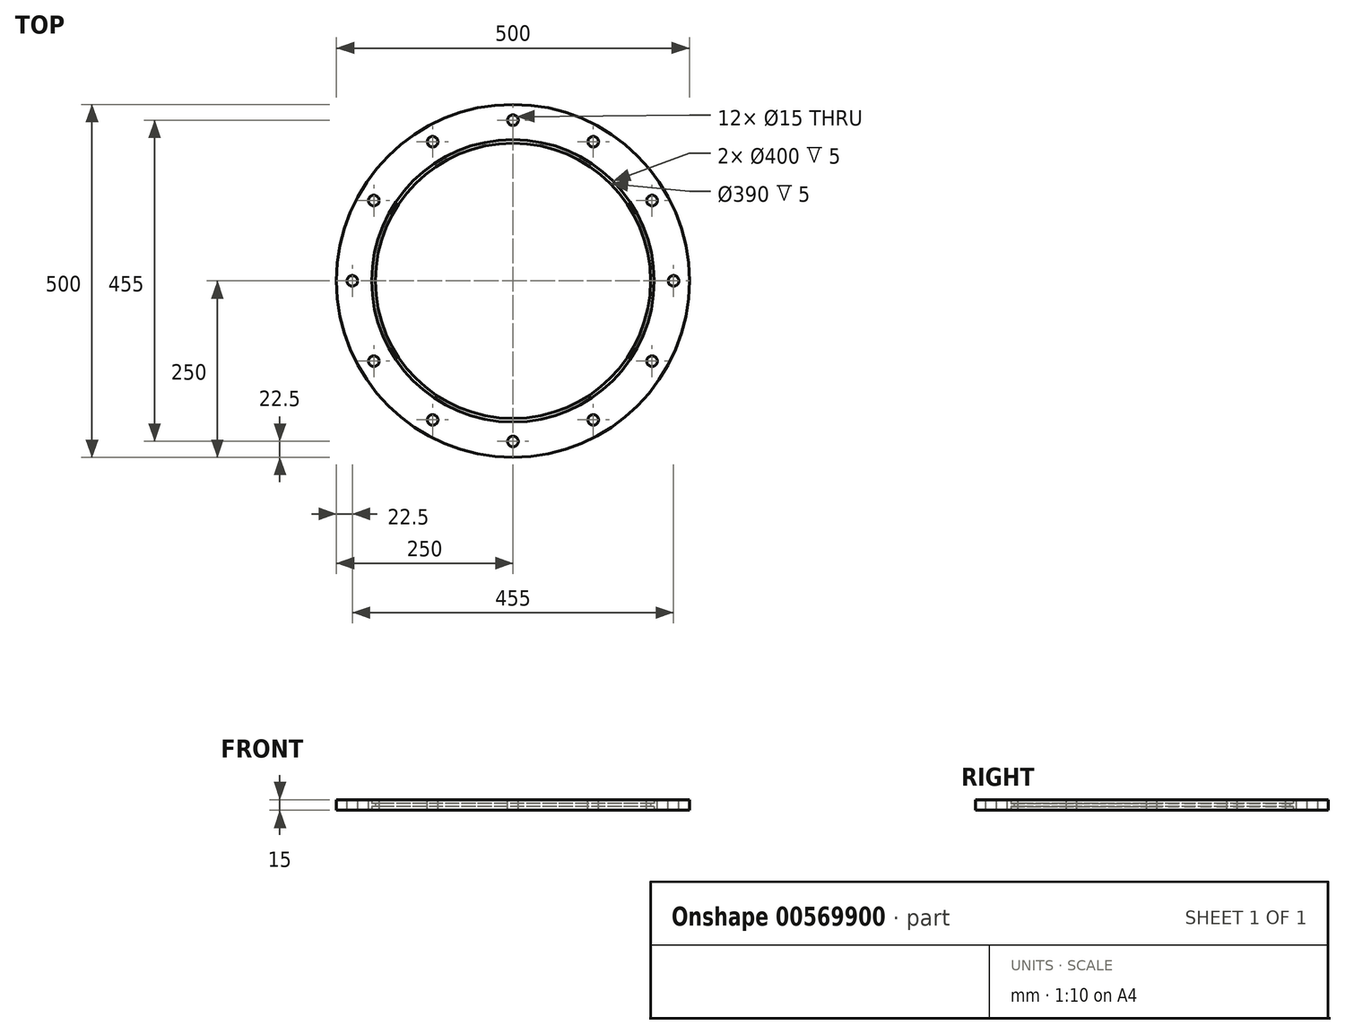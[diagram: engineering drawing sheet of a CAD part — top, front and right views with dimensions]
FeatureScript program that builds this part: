
annotation { "Feature Type Name" : "Feature", "Feature Type Description" : "" }
export const myFeature = defineFeature(function(context is Context, id is Id, definition is map)
    precondition{}
    {
        {
            var Q0;
            Q0=qCreatedBy(makeId("Top.planeOp"),FACE);
            var sketch = newSketch(context, id + "F0", { "sketchPlane" : qUnion([Q0])});
            skCircle(sketch, "E0", {"center": v(0, 0) * mm, "radius": 250 * mm});
            skCircle(sketch, "E1", {"center": v(0, 0) * mm, "radius": 200 * mm});
            skSolve(sketch);
        }
        {
            var Q0;
            Q0=qSketchRegion(id+"F0",true);
            extrude(context, id + "F1", {"entities" : qUnion([Q0]), "depth" : 15 * mm, "offsetDistance" : 25 * mm});
        }
        {
            var Q0;
            Q0=makeQuery(id+"F1.opExtrude","CAP_FACE",FACE,{"disambiguationData":[OSD([sQuery(id+"F0.wireOp",EDGE,"E0"),sQuery(id+"F0.wireOp",EDGE,"E1")])],"isStart":false});
            var sketch = newSketch(context, id + "F2", { "sketchPlane" : qUnion([Q0])});
            skCircle(sketch, "E2", {"center": v(227.5, 0) * mm, "radius": 7.5 * mm});
            skCircle(sketch, "E3.1.0", {"center": v(197.02, 113.75) * mm, "radius": 7.5 * mm});
            skCircle(sketch, "E3.2.0", {"center": v(113.75, 197.02) * mm, "radius": 7.5 * mm});
            skCircle(sketch, "E3.3.0", {"center": v(0, 227.5) * mm, "radius": 7.5 * mm});
            skCircle(sketch, "E3.4.0", {"center": v(-113.75, 197.02) * mm, "radius": 7.5 * mm});
            skCircle(sketch, "E3.5.0", {"center": v(-197.02, 113.75) * mm, "radius": 7.5 * mm});
            skCircle(sketch, "E3.6.0", {"center": v(-227.5, 0) * mm, "radius": 7.5 * mm});
            skCircle(sketch, "E3.7.0", {"center": v(-197.02, -113.75) * mm, "radius": 7.5 * mm});
            skCircle(sketch, "E3.8.0", {"center": v(-113.75, -197.02) * mm, "radius": 7.5 * mm});
            skCircle(sketch, "E3.9.0", {"center": v(0, -227.5) * mm, "radius": 7.5 * mm});
            skCircle(sketch, "E3.10.0", {"center": v(113.75, -197.02) * mm, "radius": 7.5 * mm});
            skCircle(sketch, "E3.11.0", {"center": v(197.02, -113.75) * mm, "radius": 7.5 * mm});
            skPoint(sketch, "E3.center", {"position": v(0, 0) * mm});
            skSolve(sketch);
        }
        {
            var Q0;
            Q0=qSketchRegion(id+"F2",true);
            extrude(context, id + "F3", {"entities" : qUnion([Q0]), "operationType" : NewBodyOperationType.REMOVE, "endBound" : BoundingType.UP_TO_NEXT, "oppositeDirection" : true, "depth" : 25 * mm, "offsetDistance" : 25 * mm});
        }
        {
            var Q0;
            Q0=qCreatedBy(makeId("Top.planeOp"),FACE);
            cPlane(context, id + "F4", {"entities" : qUnion([Q0]), "cplaneType" : CPlaneType.OFFSET, "offset" : 5 * mm, "width" : 150 * mm, "height" : 150 * mm});
        }
        {
            var Q0;
            Q0=qCreatedBy(id+"F4.planeOp",FACE);
            var sketch = newSketch(context, id + "F5", { "sketchPlane" : qUnion([Q0])});
            skCircle(sketch, "E4", {"center": v(0, 0) * mm, "radius": 200 * mm});
            skCircle(sketch, "E5", {"center": v(0, 0) * mm, "radius": 195 * mm});
            skSolve(sketch);
        }
        {
            var Q0;
            Q0 = qSketchRegion(id + "F5", true);
            extrude(context, id + "F6", {"entities" : qUnion([Q0]), "operationType" : NewBodyOperationType.ADD, "depth" : 5 * mm, "offsetDistance" : 25 * mm});
        }
    });
